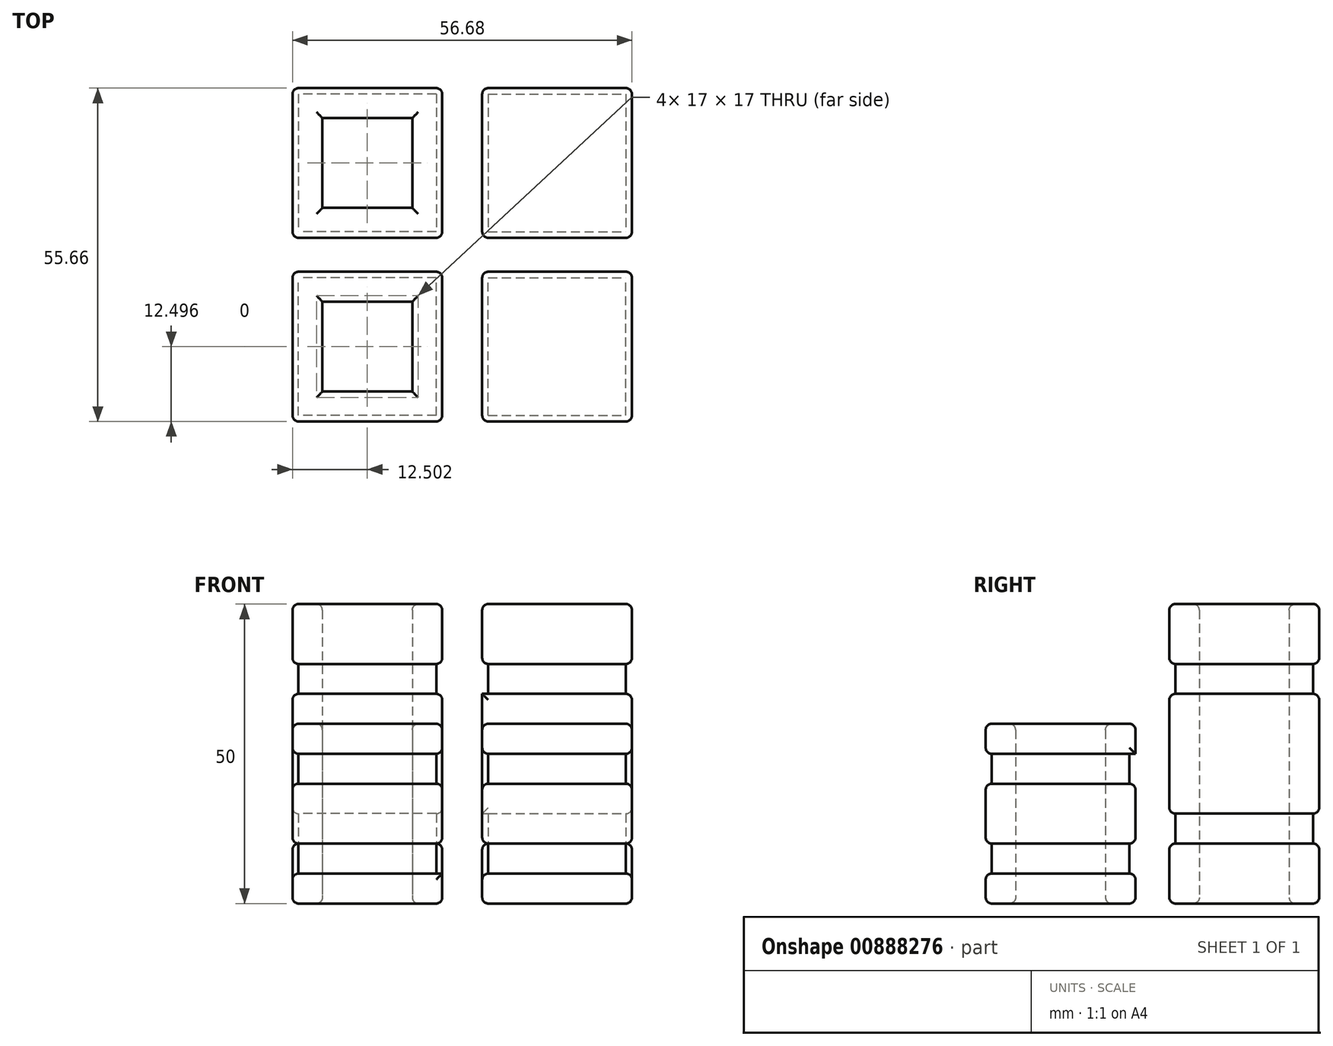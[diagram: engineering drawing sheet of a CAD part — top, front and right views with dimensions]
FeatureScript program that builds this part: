
annotation { "Feature Type Name" : "Feature", "Feature Type Description" : "" }
export const myFeature = defineFeature(function(context is Context, id is Id, definition is map)
    precondition{}
    {
        {
            var Q0;
            Q0=qCreatedBy(makeId("Top.planeOp"),FACE);
            var sketch = newSketch(context, id + "F0", { "sketchPlane" : qUnion([Q0])});
            skLineSegment(sketch, "E0.bottom", {"start": v(3.34, 2.83) * mm, "end": v(28.34, 2.83) * mm});
            skLineSegment(sketch, "E0.top", {"start": v(3.34, 27.83) * mm, "end": v(28.34, 27.83) * mm});
            skLineSegment(sketch, "E0.left", {"start": v(3.34, 2.83) * mm, "end": v(3.34, 27.83) * mm});
            skLineSegment(sketch, "E0.right", {"start": v(28.34, 2.83) * mm, "end": v(28.34, 27.83) * mm});
            skLineSegment(sketch, "E1.bottom", {"start": v(4.34, 26.83) * mm, "end": v(27.34, 26.83) * mm});
            skLineSegment(sketch, "E1.top", {"start": v(4.34, 3.83) * mm, "end": v(27.34, 3.83) * mm});
            skLineSegment(sketch, "E1.left", {"start": v(4.34, 26.83) * mm, "end": v(4.34, 3.83) * mm});
            skLineSegment(sketch, "E1.right", {"start": v(27.34, 26.83) * mm, "end": v(27.34, 3.83) * mm});
            skLineSegment(sketch, "E2.bottom", {"start": v(8.34, 22.83) * mm, "end": v(23.34, 22.83) * mm});
            skLineSegment(sketch, "E2.top", {"start": v(8.34, 7.83) * mm, "end": v(23.34, 7.83) * mm});
            skLineSegment(sketch, "E2.left", {"start": v(8.34, 22.83) * mm, "end": v(8.34, 7.83) * mm});
            skLineSegment(sketch, "E2.right", {"start": v(23.34, 22.83) * mm, "end": v(23.34, 7.83) * mm});
            skLineSegment(sketch, "E3.MirrorCS", {"start": v(-4.34, 3.83) * mm, "end": v(-27.34, 3.83) * mm});
            skLineSegment(sketch, "E4.MirrorCS", {"start": v(-3.34, 27.83) * mm, "end": v(-28.34, 27.83) * mm});
            skLineSegment(sketch, "E5.MirrorCS", {"start": v(-3.34, 2.83) * mm, "end": v(-3.34, 27.83) * mm});
            skLineSegment(sketch, "E6.MirrorCS", {"start": v(-23.34, 22.83) * mm, "end": v(-23.34, 7.83) * mm});
            skLineSegment(sketch, "E7.MirrorCS", {"start": v(-4.34, 26.83) * mm, "end": v(-27.34, 26.83) * mm});
            skLineSegment(sketch, "E8.MirrorCS", {"start": v(-27.34, 26.83) * mm, "end": v(-27.34, 3.83) * mm});
            skLineSegment(sketch, "E9.MirrorCS", {"start": v(-28.34, 2.83) * mm, "end": v(-28.34, 27.83) * mm});
            skLineSegment(sketch, "E10.MirrorCS", {"start": v(-8.34, 22.83) * mm, "end": v(-23.34, 22.83) * mm});
            skLineSegment(sketch, "E11.MirrorCS", {"start": v(-4.34, 26.83) * mm, "end": v(-4.34, 3.83) * mm});
            skLineSegment(sketch, "E12.MirrorCS", {"start": v(-8.34, 22.83) * mm, "end": v(-8.34, 7.83) * mm});
            skLineSegment(sketch, "E13.MirrorCS", {"start": v(-3.34, 2.83) * mm, "end": v(-28.34, 2.83) * mm});
            skLineSegment(sketch, "E14.MirrorCS", {"start": v(-8.34, 7.83) * mm, "end": v(-23.34, 7.83) * mm});
            skLineSegment(sketch, "E15.MirrorCS", {"start": v(-3.34, -27.83) * mm, "end": v(-28.34, -27.83) * mm});
            skLineSegment(sketch, "E16.MirrorCS", {"start": v(3.34, -2.83) * mm, "end": v(28.34, -2.83) * mm});
            skLineSegment(sketch, "E17.MirrorCS", {"start": v(3.34, -27.83) * mm, "end": v(28.34, -27.83) * mm});
            skLineSegment(sketch, "E18.MirrorCS", {"start": v(3.34, -2.83) * mm, "end": v(3.34, -27.83) * mm});
            skLineSegment(sketch, "E19.MirrorCS", {"start": v(-8.34, -7.83) * mm, "end": v(-23.34, -7.83) * mm});
            skLineSegment(sketch, "E20.MirrorCS", {"start": v(28.34, -2.83) * mm, "end": v(28.34, -27.83) * mm});
            skLineSegment(sketch, "E21.MirrorCS", {"start": v(-3.34, -2.83) * mm, "end": v(-28.34, -2.83) * mm});
            skLineSegment(sketch, "E22.MirrorCS", {"start": v(4.34, -26.83) * mm, "end": v(27.34, -26.83) * mm});
            skLineSegment(sketch, "E23.MirrorCS", {"start": v(4.34, -3.83) * mm, "end": v(27.34, -3.83) * mm});
            skLineSegment(sketch, "E24.MirrorCS", {"start": v(-8.34, -22.83) * mm, "end": v(-8.34, -7.83) * mm});
            skLineSegment(sketch, "E25.MirrorCS", {"start": v(-4.34, -26.83) * mm, "end": v(-4.34, -3.83) * mm});
            skLineSegment(sketch, "E26.MirrorCS", {"start": v(-4.34, -3.83) * mm, "end": v(-27.34, -3.83) * mm});
            skLineSegment(sketch, "E27.MirrorCS", {"start": v(-4.34, -26.83) * mm, "end": v(-27.34, -26.83) * mm});
            skLineSegment(sketch, "E28.MirrorCS", {"start": v(8.34, -7.83) * mm, "end": v(23.34, -7.83) * mm});
            skLineSegment(sketch, "E29.MirrorCS", {"start": v(23.34, -22.83) * mm, "end": v(23.34, -7.83) * mm});
            skLineSegment(sketch, "E30.MirrorCS", {"start": v(-27.34, -26.83) * mm, "end": v(-27.34, -3.83) * mm});
            skLineSegment(sketch, "E31.MirrorCS", {"start": v(-23.34, -22.83) * mm, "end": v(-23.34, -7.83) * mm});
            skLineSegment(sketch, "E32.MirrorCS", {"start": v(-3.34, -2.83) * mm, "end": v(-3.34, -27.83) * mm});
            skLineSegment(sketch, "E33.MirrorCS", {"start": v(8.34, -22.83) * mm, "end": v(8.34, -7.83) * mm});
            skLineSegment(sketch, "E34.MirrorCS", {"start": v(-8.34, -22.83) * mm, "end": v(-23.34, -22.83) * mm});
            skLineSegment(sketch, "E35.MirrorCS", {"start": v(4.34, -26.83) * mm, "end": v(4.34, -3.83) * mm});
            skLineSegment(sketch, "E36.MirrorCS", {"start": v(-28.34, -2.83) * mm, "end": v(-28.34, -27.83) * mm});
            skLineSegment(sketch, "E37.MirrorCS", {"start": v(27.34, -26.83) * mm, "end": v(27.34, -3.83) * mm});
            skLineSegment(sketch, "E38.MirrorCS", {"start": v(8.34, -22.83) * mm, "end": v(23.34, -22.83) * mm});
            skSolve(sketch);
        }
        {
            var Q0;
            Q0=makeQuery(id+"F0.imprint","IMPRINT",FACE,{"disambiguationData":[TD([[makeQuery(id+"F0.imprint","IMPRINT",EDGE,{"derivedFrom":sQuery(id+"F0.wireOp",EDGE,"E0.bottom")}),1.0]])]});
            var Q1;
            Q1=makeQuery(id+"F0.imprint","IMPRINT",FACE,{"disambiguationData":[TD([[makeQuery(id+"F0.imprint","IMPRINT",EDGE,{"derivedFrom":sQuery(id+"F0.wireOp",EDGE,"E3.MirrorCS")}),1.0]])]});
            var Q2;
            Q2=makeQuery(id+"F0.imprint","IMPRINT",FACE,{"disambiguationData":[TD([[makeQuery(id+"F0.imprint","IMPRINT",EDGE,{"derivedFrom":sQuery(id+"F0.wireOp",EDGE,"E3.MirrorCS")}),-1.0]])]});
            var Q3;
            Q3=makeQuery(id+"F0.imprint","IMPRINT",FACE,{"disambiguationData":[TD([[makeQuery(id+"F0.imprint","IMPRINT",EDGE,{"derivedFrom":sQuery(id+"F0.wireOp",EDGE,"E1.bottom")}),-1.0]])]});
            var Q4;
            Q4=makeQuery(id+"F0.imprint","IMPRINT",FACE,{"disambiguationData":[TD([[makeQuery(id+"F0.imprint","IMPRINT",EDGE,{"derivedFrom":sQuery(id+"F0.wireOp",EDGE,"E2.bottom")}),-1.0]])]});
            extrude(context, id + "F1", {"entities" : qUnion([Q0, Q1, Q2, Q3, Q4]), "depth" : 50 * mm, "offsetDistance" : 25 * mm});
        }
        {
            var Q0;
            Q0=makeQuery(id+"F0.imprint","IMPRINT",FACE,{"disambiguationData":[TD([[makeQuery(id+"F0.imprint","IMPRINT",EDGE,{"derivedFrom":sQuery(id+"F0.wireOp",EDGE,"E15.MirrorCS")}),-1.0]])]});
            var Q1;
            Q1=makeQuery(id+"F0.imprint","IMPRINT",FACE,{"disambiguationData":[TD([[makeQuery(id+"F0.imprint","IMPRINT",EDGE,{"derivedFrom":sQuery(id+"F0.wireOp",EDGE,"E19.MirrorCS")}),-1.0]])]});
            var Q2;
            Q2=makeQuery(id+"F0.imprint","IMPRINT",FACE,{"disambiguationData":[TD([[makeQuery(id+"F0.imprint","IMPRINT",EDGE,{"derivedFrom":sQuery(id+"F0.wireOp",EDGE,"E16.MirrorCS")}),-1.0]])]});
            var Q3;
            Q3=makeQuery(id+"F0.imprint","IMPRINT",FACE,{"disambiguationData":[TD([[makeQuery(id+"F0.imprint","IMPRINT",EDGE,{"derivedFrom":sQuery(id+"F0.wireOp",EDGE,"E22.MirrorCS")}),1.0]])]});
            var Q4;
            Q4=makeQuery(id+"F0.imprint","IMPRINT",FACE,{"disambiguationData":[TD([[makeQuery(id+"F0.imprint","IMPRINT",EDGE,{"derivedFrom":sQuery(id+"F0.wireOp",EDGE,"E28.MirrorCS")}),-1.0]])]});
            extrude(context, id + "F2", {"entities" : qUnion([Q0, Q1, Q2, Q3, Q4]), "depth" : 30 * mm, "offsetDistance" : 25 * mm});
        }
        {
            var Q0;
            Q0=makeQuery(id+"F0.imprint","IMPRINT",FACE,{"disambiguationData":[TD([[makeQuery(id+"F0.imprint","IMPRINT",EDGE,{"derivedFrom":sQuery(id+"F0.wireOp",EDGE,"E15.MirrorCS")}),-1.0]])]});
            var Q1;
            Q1=makeQuery(id+"F0.imprint","IMPRINT",FACE,{"disambiguationData":[TD([[makeQuery(id+"F0.imprint","IMPRINT",EDGE,{"derivedFrom":sQuery(id+"F0.wireOp",EDGE,"E16.MirrorCS")}),-1.0]])]});
            extrude(context, id + "F3", {"entities" : qUnion([Q0, Q1]), "operationType" : NewBodyOperationType.REMOVE, "depth" : 25 * mm, "offsetDistance" : 25 * mm, "hasSecondDirection" : true, "secondDirectionOppositeDirection" : false, "secondDirectionDepth" : 20 * mm});
        }
        {
            var Q0;
            Q0=makeQuery(id+"F0.imprint","IMPRINT",FACE,{"disambiguationData":[TD([[makeQuery(id+"F0.imprint","IMPRINT",EDGE,{"derivedFrom":sQuery(id+"F0.wireOp",EDGE,"E15.MirrorCS")}),-1.0]])]});
            var Q1;
            Q1=makeQuery(id+"F0.imprint","IMPRINT",FACE,{"disambiguationData":[TD([[makeQuery(id+"F0.imprint","IMPRINT",EDGE,{"derivedFrom":sQuery(id+"F0.wireOp",EDGE,"E16.MirrorCS")}),-1.0]])]});
            extrude(context, id + "F4", {"entities" : qUnion([Q0, Q1]), "operationType" : NewBodyOperationType.REMOVE, "depth" : 10 * mm, "offsetDistance" : 25 * mm, "hasSecondDirection" : true, "secondDirectionOppositeDirection" : false, "secondDirectionDepth" : 5 * mm});
        }
        {
            var Q0;
            Q0=makeQuery(id+"F0.imprint","IMPRINT",FACE,{"disambiguationData":[TD([[makeQuery(id+"F0.imprint","IMPRINT",EDGE,{"derivedFrom":sQuery(id+"F0.wireOp",EDGE,"E0.bottom")}),1.0]])]});
            var Q1;
            Q1=makeQuery(id+"F0.imprint","IMPRINT",FACE,{"disambiguationData":[TD([[makeQuery(id+"F0.imprint","IMPRINT",EDGE,{"derivedFrom":sQuery(id+"F0.wireOp",EDGE,"E3.MirrorCS")}),1.0]])]});
            extrude(context, id + "F5", {"entities" : qUnion([Q0, Q1]), "operationType" : NewBodyOperationType.REMOVE, "depth" : 40 * mm, "offsetDistance" : 25 * mm, "hasSecondDirection" : true, "secondDirectionOppositeDirection" : false, "secondDirectionDepth" : 35 * mm});
        }
        {
            var Q0;
            Q0=makeQuery(id+"F0.imprint","IMPRINT",FACE,{"disambiguationData":[TD([[makeQuery(id+"F0.imprint","IMPRINT",EDGE,{"derivedFrom":sQuery(id+"F0.wireOp",EDGE,"E0.bottom")}),1.0]])]});
            var Q1;
            Q1=makeQuery(id+"F0.imprint","IMPRINT",FACE,{"disambiguationData":[TD([[makeQuery(id+"F0.imprint","IMPRINT",EDGE,{"derivedFrom":sQuery(id+"F0.wireOp",EDGE,"E3.MirrorCS")}),1.0]])]});
            extrude(context, id + "F6", {"entities" : qUnion([Q0, Q1]), "operationType" : NewBodyOperationType.REMOVE, "depth" : 15 * mm, "offsetDistance" : 25 * mm, "hasSecondDirection" : true, "secondDirectionOppositeDirection" : false, "secondDirectionDepth" : 10 * mm});
        }
        {
            var Q0;
            {var subQ0=sQuery(id+"F0.wireOp",EDGE,"E0.right");var subQ1=sQuery(id+"F0.wireOp",EDGE,"E0.left");var subQ2=sQuery(id+"F0.wireOp",EDGE,"E0.top");var subQ3=sQuery(id+"F0.wireOp",EDGE,"E0.bottom");Q0=makeQuery(id+"F5.boolean.opBoolean","SPLIT",FACE,{"disambiguationData":[TD([makeQuery(id+"F1.opExtrude","CAP_FACE",FACE,{"disambiguationData":[OSD([subQ3,subQ2,subQ1,subQ0])],"isStart":false})])],"derivedFrom":makeQuery(id+"F1.opExtrude","SWEPT_FACE",FACE,{"disambiguationData":[OSD([subQ2])]})});}
            var Q1;
            {var subQ0=sQuery(id+"F0.wireOp",EDGE,"E0.bottom");var subQ1=sQuery(id+"F0.wireOp",EDGE,"E0.right");var subQ2=sQuery(id+"F0.wireOp",EDGE,"E0.left");var subQ3=sQuery(id+"F0.wireOp",EDGE,"E0.top");Q1=makeQuery(id+"F5.boolean.opBoolean","SPLIT",FACE,{"disambiguationData":[TD([makeQuery(id+"F1.opExtrude","CAP_FACE",FACE,{"disambiguationData":[OSD([subQ0,subQ3,subQ2,subQ1])],"isStart":false})])],"derivedFrom":makeQuery(id+"F1.opExtrude","SWEPT_FACE",FACE,{"disambiguationData":[OSD([subQ1])]})});}
            var Q2;
            {var subQ0=sQuery(id+"F0.wireOp",EDGE,"E0.right");var subQ1=sQuery(id+"F0.wireOp",EDGE,"E0.left");var subQ2=sQuery(id+"F0.wireOp",EDGE,"E0.top");var subQ3=sQuery(id+"F0.wireOp",EDGE,"E0.bottom");Q2=makeQuery(id+"F5.boolean.opBoolean","SPLIT",FACE,{"disambiguationData":[TD([makeQuery(id+"F1.opExtrude","CAP_FACE",FACE,{"disambiguationData":[OSD([subQ3,subQ2,subQ1,subQ0])],"isStart":false})])],"derivedFrom":makeQuery(id+"F1.opExtrude","SWEPT_FACE",FACE,{"disambiguationData":[OSD([subQ3])]})});}
            var Q3;
            {var subQ0=sQuery(id+"F0.wireOp",EDGE,"E0.bottom");var subQ1=sQuery(id+"F0.wireOp",EDGE,"E0.right");var subQ2=sQuery(id+"F0.wireOp",EDGE,"E0.left");var subQ3=sQuery(id+"F0.wireOp",EDGE,"E0.top");Q3=makeQuery(id+"F5.boolean.opBoolean","SPLIT",FACE,{"disambiguationData":[TD([makeQuery(id+"F1.opExtrude","CAP_FACE",FACE,{"disambiguationData":[OSD([subQ0,subQ3,subQ2,subQ1])],"isStart":false})])],"derivedFrom":makeQuery(id+"F1.opExtrude","SWEPT_FACE",FACE,{"disambiguationData":[OSD([subQ2])]})});}
            var Q4;
            {var subQ0=sQuery(id+"F0.wireOp",EDGE,"E0.bottom");var subQ2=sQuery(id+"F0.wireOp",EDGE,"E1.right");var subQ3=sQuery(id+"F0.wireOp",EDGE,"E1.left");var subQ4=sQuery(id+"F0.wireOp",EDGE,"E1.top");var subQ5=sQuery(id+"F0.wireOp",EDGE,"E1.bottom");var subQ6=sQuery(id+"F0.wireOp",EDGE,"E0.right");var subQ7=sQuery(id+"F0.wireOp",EDGE,"E0.left");var subQ8=sQuery(id+"F0.wireOp",EDGE,"E0.top");var subQ10=makeQuery(id+"F5.opExtrude","CAP_FACE",FACE,{"disambiguationData":[OSD([subQ0,subQ8,subQ7,subQ6,subQ5,subQ4,subQ3,subQ2])],"isStart":true});Q4=makeQuery(id+"F6.boolean.opBoolean","SPLIT",EDGE,{"disambiguationData":[TD([makeQuery(id+"F5.boolean.opBoolean","COPY",FACE,{"derivedFrom":subQ10})])],"derivedFrom":makeQuery(id+"F5.boolean.opBoolean","SPLIT",EDGE,{"disambiguationData":[TD([makeQuery(id+"F1.opExtrude","CAP_FACE",FACE,{"disambiguationData":[OSD([subQ0,subQ8,subQ7,subQ6])],"isStart":true})])],"derivedFrom":makeQuery(id+"F1.opExtrude","SWEPT_EDGE",EDGE,{"disambiguationData":[OSD([subQ0,subQ7])]})})});}
            var Q5;
            {var subQ0=sQuery(id+"F0.wireOp",EDGE,"E0.left");var subQ2=sQuery(id+"F0.wireOp",EDGE,"E0.right");var subQ4=sQuery(id+"F0.wireOp",EDGE,"E1.right");var subQ5=sQuery(id+"F0.wireOp",EDGE,"E1.left");var subQ6=sQuery(id+"F0.wireOp",EDGE,"E1.top");var subQ7=sQuery(id+"F0.wireOp",EDGE,"E1.bottom");var subQ8=sQuery(id+"F0.wireOp",EDGE,"E0.top");var subQ9=sQuery(id+"F0.wireOp",EDGE,"E0.bottom");var subQ10=makeQuery(id+"F5.opExtrude","CAP_FACE",FACE,{"disambiguationData":[OSD([subQ9,subQ8,subQ0,subQ2,subQ7,subQ6,subQ5,subQ4])],"isStart":true});Q5=makeQuery(id+"F6.boolean.opBoolean","SPLIT",FACE,{"disambiguationData":[TD([makeQuery(id+"F5.boolean.opBoolean","COPY",FACE,{"derivedFrom":subQ10})])],"derivedFrom":makeQuery(id+"F5.boolean.opBoolean","SPLIT",FACE,{"disambiguationData":[TD([makeQuery(id+"F1.opExtrude","CAP_FACE",FACE,{"disambiguationData":[OSD([subQ9,subQ8,subQ0,subQ2])],"isStart":true})])],"derivedFrom":makeQuery(id+"F1.opExtrude","SWEPT_FACE",FACE,{"disambiguationData":[OSD([subQ9])]})})});}
            var Q6;
            {var subQ0=sQuery(id+"F0.wireOp",EDGE,"E0.bottom");var subQ2=sQuery(id+"F0.wireOp",EDGE,"E1.right");var subQ3=sQuery(id+"F0.wireOp",EDGE,"E1.left");var subQ4=sQuery(id+"F0.wireOp",EDGE,"E1.top");var subQ5=sQuery(id+"F0.wireOp",EDGE,"E1.bottom");var subQ6=sQuery(id+"F0.wireOp",EDGE,"E0.right");var subQ7=sQuery(id+"F0.wireOp",EDGE,"E0.left");var subQ8=sQuery(id+"F0.wireOp",EDGE,"E0.top");var subQ10=makeQuery(id+"F5.opExtrude","CAP_FACE",FACE,{"disambiguationData":[OSD([subQ0,subQ8,subQ7,subQ6,subQ5,subQ4,subQ3,subQ2])],"isStart":true});Q6=makeQuery(id+"F6.boolean.opBoolean","SPLIT",FACE,{"disambiguationData":[TD([makeQuery(id+"F5.boolean.opBoolean","COPY",FACE,{"derivedFrom":subQ10})])],"derivedFrom":makeQuery(id+"F5.boolean.opBoolean","SPLIT",FACE,{"disambiguationData":[TD([makeQuery(id+"F1.opExtrude","CAP_FACE",FACE,{"disambiguationData":[OSD([subQ0,subQ8,subQ7,subQ6])],"isStart":true})])],"derivedFrom":makeQuery(id+"F1.opExtrude","SWEPT_FACE",FACE,{"disambiguationData":[OSD([subQ6])]})})});}
            var Q7;
            {var subQ0=sQuery(id+"F0.wireOp",EDGE,"E0.left");var subQ2=sQuery(id+"F0.wireOp",EDGE,"E0.right");var subQ4=sQuery(id+"F0.wireOp",EDGE,"E1.right");var subQ5=sQuery(id+"F0.wireOp",EDGE,"E1.left");var subQ6=sQuery(id+"F0.wireOp",EDGE,"E1.top");var subQ7=sQuery(id+"F0.wireOp",EDGE,"E1.bottom");var subQ8=sQuery(id+"F0.wireOp",EDGE,"E0.top");var subQ9=sQuery(id+"F0.wireOp",EDGE,"E0.bottom");var subQ10=makeQuery(id+"F5.opExtrude","CAP_FACE",FACE,{"disambiguationData":[OSD([subQ9,subQ8,subQ0,subQ2,subQ7,subQ6,subQ5,subQ4])],"isStart":true});Q7=makeQuery(id+"F6.boolean.opBoolean","SPLIT",FACE,{"disambiguationData":[TD([makeQuery(id+"F5.boolean.opBoolean","COPY",FACE,{"derivedFrom":subQ10})])],"derivedFrom":makeQuery(id+"F5.boolean.opBoolean","SPLIT",FACE,{"disambiguationData":[TD([makeQuery(id+"F1.opExtrude","CAP_FACE",FACE,{"disambiguationData":[OSD([subQ9,subQ8,subQ0,subQ2])],"isStart":true})])],"derivedFrom":makeQuery(id+"F1.opExtrude","SWEPT_FACE",FACE,{"disambiguationData":[OSD([subQ8])]})})});}
            var Q8;
            {var subQ0=sQuery(id+"F0.wireOp",EDGE,"E0.bottom");var subQ2=sQuery(id+"F0.wireOp",EDGE,"E0.right");var subQ3=sQuery(id+"F0.wireOp",EDGE,"E0.left");var subQ4=sQuery(id+"F0.wireOp",EDGE,"E0.top");var subQ5=makeQuery(id+"F1.opExtrude","CAP_FACE",FACE,{"disambiguationData":[OSD([subQ0,subQ4,subQ3,subQ2])],"isStart":true});Q8=makeQuery(id+"F6.boolean.opBoolean","SPLIT",FACE,{"disambiguationData":[TD([subQ5])],"derivedFrom":makeQuery(id+"F5.boolean.opBoolean","SPLIT",FACE,{"disambiguationData":[TD([subQ5])],"derivedFrom":makeQuery(id+"F1.opExtrude","SWEPT_FACE",FACE,{"disambiguationData":[OSD([subQ2])]})})});}
            var Q9;
            {var subQ0=sQuery(id+"F0.wireOp",EDGE,"E0.right");var subQ1=sQuery(id+"F0.wireOp",EDGE,"E0.left");var subQ2=sQuery(id+"F0.wireOp",EDGE,"E0.top");var subQ3=sQuery(id+"F0.wireOp",EDGE,"E0.bottom");var subQ4=makeQuery(id+"F1.opExtrude","CAP_FACE",FACE,{"disambiguationData":[OSD([subQ3,subQ2,subQ1,subQ0])],"isStart":true});Q9=makeQuery(id+"F6.boolean.opBoolean","SPLIT",FACE,{"disambiguationData":[TD([subQ4])],"derivedFrom":makeQuery(id+"F5.boolean.opBoolean","SPLIT",FACE,{"disambiguationData":[TD([subQ4])],"derivedFrom":makeQuery(id+"F1.opExtrude","SWEPT_FACE",FACE,{"disambiguationData":[OSD([subQ2])]})})});}
            var Q10;
            {var subQ0=sQuery(id+"F0.wireOp",EDGE,"E0.right");var subQ1=sQuery(id+"F0.wireOp",EDGE,"E0.left");var subQ2=sQuery(id+"F0.wireOp",EDGE,"E0.top");var subQ3=sQuery(id+"F0.wireOp",EDGE,"E0.bottom");var subQ4=makeQuery(id+"F1.opExtrude","CAP_FACE",FACE,{"disambiguationData":[OSD([subQ3,subQ2,subQ1,subQ0])],"isStart":true});Q10=makeQuery(id+"F6.boolean.opBoolean","SPLIT",FACE,{"disambiguationData":[TD([subQ4])],"derivedFrom":makeQuery(id+"F5.boolean.opBoolean","SPLIT",FACE,{"disambiguationData":[TD([subQ4])],"derivedFrom":makeQuery(id+"F1.opExtrude","SWEPT_FACE",FACE,{"disambiguationData":[OSD([subQ3])]})})});}
            var Q11;
            {var subQ0=sQuery(id+"F0.wireOp",EDGE,"E0.bottom");var subQ2=sQuery(id+"F0.wireOp",EDGE,"E0.right");var subQ3=sQuery(id+"F0.wireOp",EDGE,"E0.left");var subQ4=sQuery(id+"F0.wireOp",EDGE,"E0.top");var subQ5=makeQuery(id+"F1.opExtrude","CAP_FACE",FACE,{"disambiguationData":[OSD([subQ0,subQ4,subQ3,subQ2])],"isStart":true});Q11=makeQuery(id+"F6.boolean.opBoolean","SPLIT",FACE,{"disambiguationData":[TD([subQ5])],"derivedFrom":makeQuery(id+"F5.boolean.opBoolean","SPLIT",FACE,{"disambiguationData":[TD([subQ5])],"derivedFrom":makeQuery(id+"F1.opExtrude","SWEPT_FACE",FACE,{"disambiguationData":[OSD([subQ3])]})})});}
            var Q12;
            Q12=makeQuery(id+"F1.opExtrude","CAP_FACE",FACE,{"disambiguationData":[OSD([sQuery(id+"F0.wireOp",EDGE,"E4.MirrorCS"),sQuery(id+"F0.wireOp",EDGE,"E5.MirrorCS"),sQuery(id+"F0.wireOp",EDGE,"E6.MirrorCS"),sQuery(id+"F0.wireOp",EDGE,"E9.MirrorCS"),sQuery(id+"F0.wireOp",EDGE,"E10.MirrorCS"),sQuery(id+"F0.wireOp",EDGE,"E12.MirrorCS"),sQuery(id+"F0.wireOp",EDGE,"E13.MirrorCS"),sQuery(id+"F0.wireOp",EDGE,"E14.MirrorCS")])],"isStart":true});
            var Q13;
            {var subQ0=sQuery(id+"F0.wireOp",EDGE,"E4.MirrorCS");var subQ2=sQuery(id+"F0.wireOp",EDGE,"E13.MirrorCS");var subQ3=sQuery(id+"F0.wireOp",EDGE,"E9.MirrorCS");var subQ4=sQuery(id+"F0.wireOp",EDGE,"E5.MirrorCS");var subQ5=makeQuery(id+"F1.opExtrude","CAP_FACE",FACE,{"disambiguationData":[OSD([subQ0,subQ4,sQuery(id+"F0.wireOp",EDGE,"E6.MirrorCS"),subQ3,sQuery(id+"F0.wireOp",EDGE,"E10.MirrorCS"),sQuery(id+"F0.wireOp",EDGE,"E12.MirrorCS"),subQ2,sQuery(id+"F0.wireOp",EDGE,"E14.MirrorCS")])],"isStart":true});Q13=makeQuery(id+"F6.boolean.opBoolean","SPLIT",FACE,{"disambiguationData":[TD([subQ5])],"derivedFrom":makeQuery(id+"F5.boolean.opBoolean","SPLIT",FACE,{"disambiguationData":[TD([subQ5])],"derivedFrom":makeQuery(id+"F1.opExtrude","SWEPT_FACE",FACE,{"disambiguationData":[OSD([subQ3])]})})});}
            var Q14;
            {var subQ0=sQuery(id+"F0.wireOp",EDGE,"E4.MirrorCS");var subQ2=sQuery(id+"F0.wireOp",EDGE,"E13.MirrorCS");var subQ3=sQuery(id+"F0.wireOp",EDGE,"E9.MirrorCS");var subQ4=sQuery(id+"F0.wireOp",EDGE,"E5.MirrorCS");var subQ5=makeQuery(id+"F1.opExtrude","CAP_FACE",FACE,{"disambiguationData":[OSD([subQ0,subQ4,sQuery(id+"F0.wireOp",EDGE,"E6.MirrorCS"),subQ3,sQuery(id+"F0.wireOp",EDGE,"E10.MirrorCS"),sQuery(id+"F0.wireOp",EDGE,"E12.MirrorCS"),subQ2,sQuery(id+"F0.wireOp",EDGE,"E14.MirrorCS")])],"isStart":true});Q14=makeQuery(id+"F6.boolean.opBoolean","SPLIT",FACE,{"disambiguationData":[TD([subQ5])],"derivedFrom":makeQuery(id+"F5.boolean.opBoolean","SPLIT",FACE,{"disambiguationData":[TD([subQ5])],"derivedFrom":makeQuery(id+"F1.opExtrude","SWEPT_FACE",FACE,{"disambiguationData":[OSD([subQ4])]})})});}
            var Q15;
            {var subQ0=sQuery(id+"F0.wireOp",EDGE,"E13.MirrorCS");var subQ1=sQuery(id+"F0.wireOp",EDGE,"E9.MirrorCS");var subQ2=sQuery(id+"F0.wireOp",EDGE,"E5.MirrorCS");var subQ3=sQuery(id+"F0.wireOp",EDGE,"E4.MirrorCS");var subQ4=makeQuery(id+"F1.opExtrude","CAP_FACE",FACE,{"disambiguationData":[OSD([subQ3,subQ2,sQuery(id+"F0.wireOp",EDGE,"E6.MirrorCS"),subQ1,sQuery(id+"F0.wireOp",EDGE,"E10.MirrorCS"),sQuery(id+"F0.wireOp",EDGE,"E12.MirrorCS"),subQ0,sQuery(id+"F0.wireOp",EDGE,"E14.MirrorCS")])],"isStart":true});Q15=makeQuery(id+"F6.boolean.opBoolean","SPLIT",FACE,{"disambiguationData":[TD([subQ4])],"derivedFrom":makeQuery(id+"F5.boolean.opBoolean","SPLIT",FACE,{"disambiguationData":[TD([subQ4])],"derivedFrom":makeQuery(id+"F1.opExtrude","SWEPT_FACE",FACE,{"disambiguationData":[OSD([subQ3])]})})});}
            var Q16;
            {var subQ0=sQuery(id+"F0.wireOp",EDGE,"E13.MirrorCS");var subQ1=sQuery(id+"F0.wireOp",EDGE,"E9.MirrorCS");var subQ2=sQuery(id+"F0.wireOp",EDGE,"E5.MirrorCS");var subQ3=sQuery(id+"F0.wireOp",EDGE,"E4.MirrorCS");var subQ4=makeQuery(id+"F1.opExtrude","CAP_FACE",FACE,{"disambiguationData":[OSD([subQ3,subQ2,sQuery(id+"F0.wireOp",EDGE,"E6.MirrorCS"),subQ1,sQuery(id+"F0.wireOp",EDGE,"E10.MirrorCS"),sQuery(id+"F0.wireOp",EDGE,"E12.MirrorCS"),subQ0,sQuery(id+"F0.wireOp",EDGE,"E14.MirrorCS")])],"isStart":true});Q16=makeQuery(id+"F6.boolean.opBoolean","SPLIT",FACE,{"disambiguationData":[TD([subQ4])],"derivedFrom":makeQuery(id+"F5.boolean.opBoolean","SPLIT",FACE,{"disambiguationData":[TD([subQ4])],"derivedFrom":makeQuery(id+"F1.opExtrude","SWEPT_FACE",FACE,{"disambiguationData":[OSD([subQ0])]})})});}
            var Q17;
            {var subQ0=sQuery(id+"F0.wireOp",EDGE,"E5.MirrorCS");var subQ2=sQuery(id+"F0.wireOp",EDGE,"E13.MirrorCS");var subQ3=sQuery(id+"F0.wireOp",EDGE,"E11.MirrorCS");var subQ4=sQuery(id+"F0.wireOp",EDGE,"E9.MirrorCS");var subQ5=sQuery(id+"F0.wireOp",EDGE,"E8.MirrorCS");var subQ6=sQuery(id+"F0.wireOp",EDGE,"E7.MirrorCS");var subQ7=sQuery(id+"F0.wireOp",EDGE,"E4.MirrorCS");var subQ8=sQuery(id+"F0.wireOp",EDGE,"E3.MirrorCS");var subQ9=makeQuery(id+"F5.opExtrude","CAP_FACE",FACE,{"disambiguationData":[OSD([subQ8,subQ7,subQ0,subQ6,subQ5,subQ4,subQ3,subQ2])],"isStart":true});Q17=makeQuery(id+"F6.boolean.opBoolean","SPLIT",FACE,{"disambiguationData":[TD([makeQuery(id+"F5.boolean.opBoolean","COPY",FACE,{"derivedFrom":subQ9})])],"derivedFrom":makeQuery(id+"F5.boolean.opBoolean","SPLIT",FACE,{"disambiguationData":[TD([makeQuery(id+"F1.opExtrude","CAP_FACE",FACE,{"disambiguationData":[OSD([subQ7,subQ0,sQuery(id+"F0.wireOp",EDGE,"E6.MirrorCS"),subQ4,sQuery(id+"F0.wireOp",EDGE,"E10.MirrorCS"),sQuery(id+"F0.wireOp",EDGE,"E12.MirrorCS"),subQ2,sQuery(id+"F0.wireOp",EDGE,"E14.MirrorCS")])],"isStart":true})])],"derivedFrom":makeQuery(id+"F1.opExtrude","SWEPT_FACE",FACE,{"disambiguationData":[OSD([subQ2])]})})});}
            var Q18;
            {var subQ0=sQuery(id+"F0.wireOp",EDGE,"E4.MirrorCS");var subQ2=sQuery(id+"F0.wireOp",EDGE,"E13.MirrorCS");var subQ4=sQuery(id+"F0.wireOp",EDGE,"E11.MirrorCS");var subQ5=sQuery(id+"F0.wireOp",EDGE,"E9.MirrorCS");var subQ6=sQuery(id+"F0.wireOp",EDGE,"E8.MirrorCS");var subQ7=sQuery(id+"F0.wireOp",EDGE,"E7.MirrorCS");var subQ8=sQuery(id+"F0.wireOp",EDGE,"E5.MirrorCS");var subQ9=sQuery(id+"F0.wireOp",EDGE,"E3.MirrorCS");var subQ10=makeQuery(id+"F5.opExtrude","CAP_FACE",FACE,{"disambiguationData":[OSD([subQ9,subQ0,subQ8,subQ7,subQ6,subQ5,subQ4,subQ2])],"isStart":true});Q18=makeQuery(id+"F6.boolean.opBoolean","SPLIT",FACE,{"disambiguationData":[TD([makeQuery(id+"F5.boolean.opBoolean","COPY",FACE,{"derivedFrom":subQ10})])],"derivedFrom":makeQuery(id+"F5.boolean.opBoolean","SPLIT",FACE,{"disambiguationData":[TD([makeQuery(id+"F1.opExtrude","CAP_FACE",FACE,{"disambiguationData":[OSD([subQ0,subQ8,sQuery(id+"F0.wireOp",EDGE,"E6.MirrorCS"),subQ5,sQuery(id+"F0.wireOp",EDGE,"E10.MirrorCS"),sQuery(id+"F0.wireOp",EDGE,"E12.MirrorCS"),subQ2,sQuery(id+"F0.wireOp",EDGE,"E14.MirrorCS")])],"isStart":true})])],"derivedFrom":makeQuery(id+"F1.opExtrude","SWEPT_FACE",FACE,{"disambiguationData":[OSD([subQ5])]})})});}
            var Q19;
            {var subQ0=sQuery(id+"F0.wireOp",EDGE,"E13.MirrorCS");var subQ1=sQuery(id+"F0.wireOp",EDGE,"E9.MirrorCS");var subQ2=sQuery(id+"F0.wireOp",EDGE,"E5.MirrorCS");var subQ3=sQuery(id+"F0.wireOp",EDGE,"E4.MirrorCS");Q19=makeQuery(id+"F5.boolean.opBoolean","SPLIT",FACE,{"disambiguationData":[TD([makeQuery(id+"F1.opExtrude","CAP_FACE",FACE,{"disambiguationData":[OSD([subQ3,subQ2,sQuery(id+"F0.wireOp",EDGE,"E6.MirrorCS"),subQ1,sQuery(id+"F0.wireOp",EDGE,"E10.MirrorCS"),sQuery(id+"F0.wireOp",EDGE,"E12.MirrorCS"),subQ0,sQuery(id+"F0.wireOp",EDGE,"E14.MirrorCS")])],"isStart":false})])],"derivedFrom":makeQuery(id+"F1.opExtrude","SWEPT_FACE",FACE,{"disambiguationData":[OSD([subQ0])]})});}
            var Q20;
            {var subQ0=sQuery(id+"F0.wireOp",EDGE,"E4.MirrorCS");var subQ1=sQuery(id+"F0.wireOp",EDGE,"E13.MirrorCS");var subQ2=sQuery(id+"F0.wireOp",EDGE,"E9.MirrorCS");var subQ3=sQuery(id+"F0.wireOp",EDGE,"E5.MirrorCS");Q20=makeQuery(id+"F5.boolean.opBoolean","SPLIT",FACE,{"disambiguationData":[TD([makeQuery(id+"F1.opExtrude","CAP_FACE",FACE,{"disambiguationData":[OSD([subQ0,subQ3,sQuery(id+"F0.wireOp",EDGE,"E6.MirrorCS"),subQ2,sQuery(id+"F0.wireOp",EDGE,"E10.MirrorCS"),sQuery(id+"F0.wireOp",EDGE,"E12.MirrorCS"),subQ1,sQuery(id+"F0.wireOp",EDGE,"E14.MirrorCS")])],"isStart":false})])],"derivedFrom":makeQuery(id+"F1.opExtrude","SWEPT_FACE",FACE,{"disambiguationData":[OSD([subQ2])]})});}
            var Q21;
            Q21=makeQuery(id+"F1.opExtrude","CAP_FACE",FACE,{"disambiguationData":[OSD([sQuery(id+"F0.wireOp",EDGE,"E4.MirrorCS"),sQuery(id+"F0.wireOp",EDGE,"E5.MirrorCS"),sQuery(id+"F0.wireOp",EDGE,"E6.MirrorCS"),sQuery(id+"F0.wireOp",EDGE,"E9.MirrorCS"),sQuery(id+"F0.wireOp",EDGE,"E10.MirrorCS"),sQuery(id+"F0.wireOp",EDGE,"E12.MirrorCS"),sQuery(id+"F0.wireOp",EDGE,"E13.MirrorCS"),sQuery(id+"F0.wireOp",EDGE,"E14.MirrorCS")])],"isStart":false});
            var Q22;
            {var subQ0=sQuery(id+"F0.wireOp",EDGE,"E5.MirrorCS");var subQ2=sQuery(id+"F0.wireOp",EDGE,"E13.MirrorCS");var subQ3=sQuery(id+"F0.wireOp",EDGE,"E11.MirrorCS");var subQ4=sQuery(id+"F0.wireOp",EDGE,"E9.MirrorCS");var subQ5=sQuery(id+"F0.wireOp",EDGE,"E8.MirrorCS");var subQ6=sQuery(id+"F0.wireOp",EDGE,"E7.MirrorCS");var subQ7=sQuery(id+"F0.wireOp",EDGE,"E4.MirrorCS");var subQ8=sQuery(id+"F0.wireOp",EDGE,"E3.MirrorCS");var subQ9=makeQuery(id+"F5.opExtrude","CAP_FACE",FACE,{"disambiguationData":[OSD([subQ8,subQ7,subQ0,subQ6,subQ5,subQ4,subQ3,subQ2])],"isStart":true});Q22=makeQuery(id+"F6.boolean.opBoolean","SPLIT",FACE,{"disambiguationData":[TD([makeQuery(id+"F5.boolean.opBoolean","COPY",FACE,{"derivedFrom":subQ9})])],"derivedFrom":makeQuery(id+"F5.boolean.opBoolean","SPLIT",FACE,{"disambiguationData":[TD([makeQuery(id+"F1.opExtrude","CAP_FACE",FACE,{"disambiguationData":[OSD([subQ7,subQ0,sQuery(id+"F0.wireOp",EDGE,"E6.MirrorCS"),subQ4,sQuery(id+"F0.wireOp",EDGE,"E10.MirrorCS"),sQuery(id+"F0.wireOp",EDGE,"E12.MirrorCS"),subQ2,sQuery(id+"F0.wireOp",EDGE,"E14.MirrorCS")])],"isStart":true})])],"derivedFrom":makeQuery(id+"F1.opExtrude","SWEPT_FACE",FACE,{"disambiguationData":[OSD([subQ7])]})})});}
            var Q23;
            {var subQ0=sQuery(id+"F0.wireOp",EDGE,"E4.MirrorCS");var subQ2=sQuery(id+"F0.wireOp",EDGE,"E13.MirrorCS");var subQ4=sQuery(id+"F0.wireOp",EDGE,"E11.MirrorCS");var subQ5=sQuery(id+"F0.wireOp",EDGE,"E9.MirrorCS");var subQ6=sQuery(id+"F0.wireOp",EDGE,"E8.MirrorCS");var subQ7=sQuery(id+"F0.wireOp",EDGE,"E7.MirrorCS");var subQ8=sQuery(id+"F0.wireOp",EDGE,"E5.MirrorCS");var subQ9=sQuery(id+"F0.wireOp",EDGE,"E3.MirrorCS");var subQ10=makeQuery(id+"F5.opExtrude","CAP_FACE",FACE,{"disambiguationData":[OSD([subQ9,subQ0,subQ8,subQ7,subQ6,subQ5,subQ4,subQ2])],"isStart":true});Q23=makeQuery(id+"F6.boolean.opBoolean","SPLIT",FACE,{"disambiguationData":[TD([makeQuery(id+"F5.boolean.opBoolean","COPY",FACE,{"derivedFrom":subQ10})])],"derivedFrom":makeQuery(id+"F5.boolean.opBoolean","SPLIT",FACE,{"disambiguationData":[TD([makeQuery(id+"F1.opExtrude","CAP_FACE",FACE,{"disambiguationData":[OSD([subQ0,subQ8,sQuery(id+"F0.wireOp",EDGE,"E6.MirrorCS"),subQ5,sQuery(id+"F0.wireOp",EDGE,"E10.MirrorCS"),sQuery(id+"F0.wireOp",EDGE,"E12.MirrorCS"),subQ2,sQuery(id+"F0.wireOp",EDGE,"E14.MirrorCS")])],"isStart":true})])],"derivedFrom":makeQuery(id+"F1.opExtrude","SWEPT_FACE",FACE,{"disambiguationData":[OSD([subQ8])]})})});}
            var Q24;
            {var subQ0=sQuery(id+"F0.wireOp",EDGE,"E13.MirrorCS");var subQ1=sQuery(id+"F0.wireOp",EDGE,"E9.MirrorCS");var subQ2=sQuery(id+"F0.wireOp",EDGE,"E5.MirrorCS");var subQ3=sQuery(id+"F0.wireOp",EDGE,"E4.MirrorCS");Q24=makeQuery(id+"F5.boolean.opBoolean","SPLIT",FACE,{"disambiguationData":[TD([makeQuery(id+"F1.opExtrude","CAP_FACE",FACE,{"disambiguationData":[OSD([subQ3,subQ2,sQuery(id+"F0.wireOp",EDGE,"E6.MirrorCS"),subQ1,sQuery(id+"F0.wireOp",EDGE,"E10.MirrorCS"),sQuery(id+"F0.wireOp",EDGE,"E12.MirrorCS"),subQ0,sQuery(id+"F0.wireOp",EDGE,"E14.MirrorCS")])],"isStart":false})])],"derivedFrom":makeQuery(id+"F1.opExtrude","SWEPT_FACE",FACE,{"disambiguationData":[OSD([subQ3])]})});}
            var Q25;
            {var subQ0=sQuery(id+"F0.wireOp",EDGE,"E4.MirrorCS");var subQ1=sQuery(id+"F0.wireOp",EDGE,"E13.MirrorCS");var subQ2=sQuery(id+"F0.wireOp",EDGE,"E9.MirrorCS");var subQ3=sQuery(id+"F0.wireOp",EDGE,"E5.MirrorCS");Q25=makeQuery(id+"F5.boolean.opBoolean","SPLIT",FACE,{"disambiguationData":[TD([makeQuery(id+"F1.opExtrude","CAP_FACE",FACE,{"disambiguationData":[OSD([subQ0,subQ3,sQuery(id+"F0.wireOp",EDGE,"E6.MirrorCS"),subQ2,sQuery(id+"F0.wireOp",EDGE,"E10.MirrorCS"),sQuery(id+"F0.wireOp",EDGE,"E12.MirrorCS"),subQ1,sQuery(id+"F0.wireOp",EDGE,"E14.MirrorCS")])],"isStart":false})])],"derivedFrom":makeQuery(id+"F1.opExtrude","SWEPT_FACE",FACE,{"disambiguationData":[OSD([subQ3])]})});}
            fillet(context, id + "F7", {"entities" : qUnion([Q0, Q1, Q2, Q3, Q4, Q5, Q6, Q7, Q8, Q9, Q10, Q11, Q12, Q13, Q14, Q15, Q16, Q17, Q18, Q19, Q20, Q21, Q22, Q23, Q24, Q25]), "radius" : 1 * mm, "tangentPropagation" : true, "allowEdgeOverflow" : false});
        }
        {
            var Q0;
            {var subQ0=sQuery(id+"F0.wireOp",EDGE,"E32.MirrorCS");var subQ2=sQuery(id+"F0.wireOp",EDGE,"E36.MirrorCS");var subQ4=sQuery(id+"F0.wireOp",EDGE,"E30.MirrorCS");var subQ5=sQuery(id+"F0.wireOp",EDGE,"E27.MirrorCS");var subQ6=sQuery(id+"F0.wireOp",EDGE,"E26.MirrorCS");var subQ7=sQuery(id+"F0.wireOp",EDGE,"E25.MirrorCS");var subQ8=sQuery(id+"F0.wireOp",EDGE,"E21.MirrorCS");var subQ9=sQuery(id+"F0.wireOp",EDGE,"E15.MirrorCS");var subQ10=makeQuery(id+"F3.opExtrude","CAP_FACE",FACE,{"disambiguationData":[OSD([subQ9,subQ8,subQ7,subQ6,subQ5,subQ4,subQ0,subQ2])],"isStart":true});Q0=makeQuery(id+"F4.boolean.opBoolean","SPLIT",FACE,{"disambiguationData":[TD([makeQuery(id+"F3.boolean.opBoolean","COPY",FACE,{"derivedFrom":subQ10})])],"derivedFrom":makeQuery(id+"F3.boolean.opBoolean","SPLIT",FACE,{"disambiguationData":[TD([makeQuery(id+"F2.opExtrude","CAP_FACE",FACE,{"disambiguationData":[OSD([subQ9,sQuery(id+"F0.wireOp",EDGE,"E19.MirrorCS"),subQ8,sQuery(id+"F0.wireOp",EDGE,"E24.MirrorCS"),sQuery(id+"F0.wireOp",EDGE,"E31.MirrorCS"),subQ0,sQuery(id+"F0.wireOp",EDGE,"E34.MirrorCS"),subQ2])],"isStart":true})])],"derivedFrom":makeQuery(id+"F2.opExtrude","SWEPT_FACE",FACE,{"disambiguationData":[OSD([subQ8])]})})});}
            var Q1;
            {var subQ0=sQuery(id+"F0.wireOp",EDGE,"E15.MirrorCS");var subQ2=sQuery(id+"F0.wireOp",EDGE,"E21.MirrorCS");var subQ4=sQuery(id+"F0.wireOp",EDGE,"E36.MirrorCS");var subQ5=sQuery(id+"F0.wireOp",EDGE,"E32.MirrorCS");var subQ6=sQuery(id+"F0.wireOp",EDGE,"E30.MirrorCS");var subQ7=sQuery(id+"F0.wireOp",EDGE,"E27.MirrorCS");var subQ8=sQuery(id+"F0.wireOp",EDGE,"E26.MirrorCS");var subQ9=sQuery(id+"F0.wireOp",EDGE,"E25.MirrorCS");var subQ10=makeQuery(id+"F3.opExtrude","CAP_FACE",FACE,{"disambiguationData":[OSD([subQ0,subQ2,subQ9,subQ8,subQ7,subQ6,subQ5,subQ4])],"isStart":true});Q1=makeQuery(id+"F4.boolean.opBoolean","SPLIT",FACE,{"disambiguationData":[TD([makeQuery(id+"F3.boolean.opBoolean","COPY",FACE,{"derivedFrom":subQ10})])],"derivedFrom":makeQuery(id+"F3.boolean.opBoolean","SPLIT",FACE,{"disambiguationData":[TD([makeQuery(id+"F2.opExtrude","CAP_FACE",FACE,{"disambiguationData":[OSD([subQ0,sQuery(id+"F0.wireOp",EDGE,"E19.MirrorCS"),subQ2,sQuery(id+"F0.wireOp",EDGE,"E24.MirrorCS"),sQuery(id+"F0.wireOp",EDGE,"E31.MirrorCS"),subQ5,sQuery(id+"F0.wireOp",EDGE,"E34.MirrorCS"),subQ4])],"isStart":true})])],"derivedFrom":makeQuery(id+"F2.opExtrude","SWEPT_FACE",FACE,{"disambiguationData":[OSD([subQ5])]})})});}
            var Q2;
            {var subQ0=sQuery(id+"F0.wireOp",EDGE,"E36.MirrorCS");var subQ1=sQuery(id+"F0.wireOp",EDGE,"E32.MirrorCS");var subQ2=sQuery(id+"F0.wireOp",EDGE,"E21.MirrorCS");var subQ3=sQuery(id+"F0.wireOp",EDGE,"E15.MirrorCS");Q2=makeQuery(id+"F3.boolean.opBoolean","SPLIT",FACE,{"disambiguationData":[TD([makeQuery(id+"F2.opExtrude","CAP_FACE",FACE,{"disambiguationData":[OSD([subQ3,sQuery(id+"F0.wireOp",EDGE,"E19.MirrorCS"),subQ2,sQuery(id+"F0.wireOp",EDGE,"E24.MirrorCS"),sQuery(id+"F0.wireOp",EDGE,"E31.MirrorCS"),subQ1,sQuery(id+"F0.wireOp",EDGE,"E34.MirrorCS"),subQ0])],"isStart":false})])],"derivedFrom":makeQuery(id+"F2.opExtrude","SWEPT_FACE",FACE,{"disambiguationData":[OSD([subQ2])]})});}
            var Q3;
            {var subQ0=sQuery(id+"F0.wireOp",EDGE,"E15.MirrorCS");var subQ1=sQuery(id+"F0.wireOp",EDGE,"E21.MirrorCS");var subQ2=sQuery(id+"F0.wireOp",EDGE,"E36.MirrorCS");var subQ3=sQuery(id+"F0.wireOp",EDGE,"E32.MirrorCS");Q3=makeQuery(id+"F3.boolean.opBoolean","SPLIT",FACE,{"disambiguationData":[TD([makeQuery(id+"F2.opExtrude","CAP_FACE",FACE,{"disambiguationData":[OSD([subQ0,sQuery(id+"F0.wireOp",EDGE,"E19.MirrorCS"),subQ1,sQuery(id+"F0.wireOp",EDGE,"E24.MirrorCS"),sQuery(id+"F0.wireOp",EDGE,"E31.MirrorCS"),subQ3,sQuery(id+"F0.wireOp",EDGE,"E34.MirrorCS"),subQ2])],"isStart":false})])],"derivedFrom":makeQuery(id+"F2.opExtrude","SWEPT_FACE",FACE,{"disambiguationData":[OSD([subQ3])]})});}
            var Q4;
            Q4=makeQuery(id+"F2.opExtrude","CAP_FACE",FACE,{"disambiguationData":[OSD([sQuery(id+"F0.wireOp",EDGE,"E15.MirrorCS"),sQuery(id+"F0.wireOp",EDGE,"E19.MirrorCS"),sQuery(id+"F0.wireOp",EDGE,"E21.MirrorCS"),sQuery(id+"F0.wireOp",EDGE,"E24.MirrorCS"),sQuery(id+"F0.wireOp",EDGE,"E31.MirrorCS"),sQuery(id+"F0.wireOp",EDGE,"E32.MirrorCS"),sQuery(id+"F0.wireOp",EDGE,"E34.MirrorCS"),sQuery(id+"F0.wireOp",EDGE,"E36.MirrorCS")])],"isStart":false});
            var Q5;
            {var subQ0=sQuery(id+"F0.wireOp",EDGE,"E36.MirrorCS");var subQ1=sQuery(id+"F0.wireOp",EDGE,"E32.MirrorCS");var subQ2=sQuery(id+"F0.wireOp",EDGE,"E21.MirrorCS");var subQ3=sQuery(id+"F0.wireOp",EDGE,"E15.MirrorCS");var subQ4=makeQuery(id+"F2.opExtrude","CAP_FACE",FACE,{"disambiguationData":[OSD([subQ3,sQuery(id+"F0.wireOp",EDGE,"E19.MirrorCS"),subQ2,sQuery(id+"F0.wireOp",EDGE,"E24.MirrorCS"),sQuery(id+"F0.wireOp",EDGE,"E31.MirrorCS"),subQ1,sQuery(id+"F0.wireOp",EDGE,"E34.MirrorCS"),subQ0])],"isStart":true});Q5=makeQuery(id+"F4.boolean.opBoolean","SPLIT",FACE,{"disambiguationData":[TD([subQ4])],"derivedFrom":makeQuery(id+"F3.boolean.opBoolean","SPLIT",FACE,{"disambiguationData":[TD([subQ4])],"derivedFrom":makeQuery(id+"F2.opExtrude","SWEPT_FACE",FACE,{"disambiguationData":[OSD([subQ2])]})})});}
            var Q6;
            {var subQ0=sQuery(id+"F0.wireOp",EDGE,"E15.MirrorCS");var subQ2=sQuery(id+"F0.wireOp",EDGE,"E21.MirrorCS");var subQ4=sQuery(id+"F0.wireOp",EDGE,"E36.MirrorCS");var subQ5=sQuery(id+"F0.wireOp",EDGE,"E32.MirrorCS");var subQ6=makeQuery(id+"F2.opExtrude","CAP_FACE",FACE,{"disambiguationData":[OSD([subQ0,sQuery(id+"F0.wireOp",EDGE,"E19.MirrorCS"),subQ2,sQuery(id+"F0.wireOp",EDGE,"E24.MirrorCS"),sQuery(id+"F0.wireOp",EDGE,"E31.MirrorCS"),subQ5,sQuery(id+"F0.wireOp",EDGE,"E34.MirrorCS"),subQ4])],"isStart":true});Q6=makeQuery(id+"F4.boolean.opBoolean","SPLIT",FACE,{"disambiguationData":[TD([subQ6])],"derivedFrom":makeQuery(id+"F3.boolean.opBoolean","SPLIT",FACE,{"disambiguationData":[TD([subQ6])],"derivedFrom":makeQuery(id+"F2.opExtrude","SWEPT_FACE",FACE,{"disambiguationData":[OSD([subQ4])]})})});}
            var Q7;
            {var subQ0=sQuery(id+"F0.wireOp",EDGE,"E15.MirrorCS");var subQ2=sQuery(id+"F0.wireOp",EDGE,"E21.MirrorCS");var subQ4=sQuery(id+"F0.wireOp",EDGE,"E36.MirrorCS");var subQ5=sQuery(id+"F0.wireOp",EDGE,"E32.MirrorCS");var subQ6=sQuery(id+"F0.wireOp",EDGE,"E30.MirrorCS");var subQ7=sQuery(id+"F0.wireOp",EDGE,"E27.MirrorCS");var subQ8=sQuery(id+"F0.wireOp",EDGE,"E26.MirrorCS");var subQ9=sQuery(id+"F0.wireOp",EDGE,"E25.MirrorCS");var subQ10=makeQuery(id+"F3.opExtrude","CAP_FACE",FACE,{"disambiguationData":[OSD([subQ0,subQ2,subQ9,subQ8,subQ7,subQ6,subQ5,subQ4])],"isStart":true});Q7=makeQuery(id+"F4.boolean.opBoolean","SPLIT",FACE,{"disambiguationData":[TD([makeQuery(id+"F3.boolean.opBoolean","COPY",FACE,{"derivedFrom":subQ10})])],"derivedFrom":makeQuery(id+"F3.boolean.opBoolean","SPLIT",FACE,{"disambiguationData":[TD([makeQuery(id+"F2.opExtrude","CAP_FACE",FACE,{"disambiguationData":[OSD([subQ0,sQuery(id+"F0.wireOp",EDGE,"E19.MirrorCS"),subQ2,sQuery(id+"F0.wireOp",EDGE,"E24.MirrorCS"),sQuery(id+"F0.wireOp",EDGE,"E31.MirrorCS"),subQ5,sQuery(id+"F0.wireOp",EDGE,"E34.MirrorCS"),subQ4])],"isStart":true})])],"derivedFrom":makeQuery(id+"F2.opExtrude","SWEPT_FACE",FACE,{"disambiguationData":[OSD([subQ4])]})})});}
            var Q8;
            {var subQ0=sQuery(id+"F0.wireOp",EDGE,"E32.MirrorCS");var subQ2=sQuery(id+"F0.wireOp",EDGE,"E36.MirrorCS");var subQ4=sQuery(id+"F0.wireOp",EDGE,"E30.MirrorCS");var subQ5=sQuery(id+"F0.wireOp",EDGE,"E27.MirrorCS");var subQ6=sQuery(id+"F0.wireOp",EDGE,"E26.MirrorCS");var subQ7=sQuery(id+"F0.wireOp",EDGE,"E25.MirrorCS");var subQ8=sQuery(id+"F0.wireOp",EDGE,"E21.MirrorCS");var subQ9=sQuery(id+"F0.wireOp",EDGE,"E15.MirrorCS");var subQ10=makeQuery(id+"F3.opExtrude","CAP_FACE",FACE,{"disambiguationData":[OSD([subQ9,subQ8,subQ7,subQ6,subQ5,subQ4,subQ0,subQ2])],"isStart":true});Q8=makeQuery(id+"F4.boolean.opBoolean","SPLIT",FACE,{"disambiguationData":[TD([makeQuery(id+"F3.boolean.opBoolean","COPY",FACE,{"derivedFrom":subQ10})])],"derivedFrom":makeQuery(id+"F3.boolean.opBoolean","SPLIT",FACE,{"disambiguationData":[TD([makeQuery(id+"F2.opExtrude","CAP_FACE",FACE,{"disambiguationData":[OSD([subQ9,sQuery(id+"F0.wireOp",EDGE,"E19.MirrorCS"),subQ8,sQuery(id+"F0.wireOp",EDGE,"E24.MirrorCS"),sQuery(id+"F0.wireOp",EDGE,"E31.MirrorCS"),subQ0,sQuery(id+"F0.wireOp",EDGE,"E34.MirrorCS"),subQ2])],"isStart":true})])],"derivedFrom":makeQuery(id+"F2.opExtrude","SWEPT_FACE",FACE,{"disambiguationData":[OSD([subQ9])]})})});}
            var Q9;
            {var subQ0=sQuery(id+"F0.wireOp",EDGE,"E36.MirrorCS");var subQ1=sQuery(id+"F0.wireOp",EDGE,"E32.MirrorCS");var subQ2=sQuery(id+"F0.wireOp",EDGE,"E21.MirrorCS");var subQ3=sQuery(id+"F0.wireOp",EDGE,"E15.MirrorCS");var subQ4=makeQuery(id+"F2.opExtrude","CAP_FACE",FACE,{"disambiguationData":[OSD([subQ3,sQuery(id+"F0.wireOp",EDGE,"E19.MirrorCS"),subQ2,sQuery(id+"F0.wireOp",EDGE,"E24.MirrorCS"),sQuery(id+"F0.wireOp",EDGE,"E31.MirrorCS"),subQ1,sQuery(id+"F0.wireOp",EDGE,"E34.MirrorCS"),subQ0])],"isStart":true});Q9=makeQuery(id+"F4.boolean.opBoolean","SPLIT",FACE,{"disambiguationData":[TD([subQ4])],"derivedFrom":makeQuery(id+"F3.boolean.opBoolean","SPLIT",FACE,{"disambiguationData":[TD([subQ4])],"derivedFrom":makeQuery(id+"F2.opExtrude","SWEPT_FACE",FACE,{"disambiguationData":[OSD([subQ3])]})})});}
            var Q10;
            Q10=makeQuery(id+"F2.opExtrude","CAP_FACE",FACE,{"disambiguationData":[OSD([sQuery(id+"F0.wireOp",EDGE,"E15.MirrorCS"),sQuery(id+"F0.wireOp",EDGE,"E19.MirrorCS"),sQuery(id+"F0.wireOp",EDGE,"E21.MirrorCS"),sQuery(id+"F0.wireOp",EDGE,"E24.MirrorCS"),sQuery(id+"F0.wireOp",EDGE,"E31.MirrorCS"),sQuery(id+"F0.wireOp",EDGE,"E32.MirrorCS"),sQuery(id+"F0.wireOp",EDGE,"E34.MirrorCS"),sQuery(id+"F0.wireOp",EDGE,"E36.MirrorCS")])],"isStart":true});
            var Q11;
            {var subQ0=sQuery(id+"F0.wireOp",EDGE,"E15.MirrorCS");var subQ1=sQuery(id+"F0.wireOp",EDGE,"E21.MirrorCS");var subQ2=sQuery(id+"F0.wireOp",EDGE,"E36.MirrorCS");var subQ3=sQuery(id+"F0.wireOp",EDGE,"E32.MirrorCS");Q11=makeQuery(id+"F3.boolean.opBoolean","SPLIT",FACE,{"disambiguationData":[TD([makeQuery(id+"F2.opExtrude","CAP_FACE",FACE,{"disambiguationData":[OSD([subQ0,sQuery(id+"F0.wireOp",EDGE,"E19.MirrorCS"),subQ1,sQuery(id+"F0.wireOp",EDGE,"E24.MirrorCS"),sQuery(id+"F0.wireOp",EDGE,"E31.MirrorCS"),subQ3,sQuery(id+"F0.wireOp",EDGE,"E34.MirrorCS"),subQ2])],"isStart":false})])],"derivedFrom":makeQuery(id+"F2.opExtrude","SWEPT_FACE",FACE,{"disambiguationData":[OSD([subQ2])]})});}
            var Q12;
            {var subQ0=sQuery(id+"F0.wireOp",EDGE,"E36.MirrorCS");var subQ1=sQuery(id+"F0.wireOp",EDGE,"E32.MirrorCS");var subQ2=sQuery(id+"F0.wireOp",EDGE,"E21.MirrorCS");var subQ3=sQuery(id+"F0.wireOp",EDGE,"E15.MirrorCS");Q12=makeQuery(id+"F3.boolean.opBoolean","SPLIT",FACE,{"disambiguationData":[TD([makeQuery(id+"F2.opExtrude","CAP_FACE",FACE,{"disambiguationData":[OSD([subQ3,sQuery(id+"F0.wireOp",EDGE,"E19.MirrorCS"),subQ2,sQuery(id+"F0.wireOp",EDGE,"E24.MirrorCS"),sQuery(id+"F0.wireOp",EDGE,"E31.MirrorCS"),subQ1,sQuery(id+"F0.wireOp",EDGE,"E34.MirrorCS"),subQ0])],"isStart":false})])],"derivedFrom":makeQuery(id+"F2.opExtrude","SWEPT_FACE",FACE,{"disambiguationData":[OSD([subQ3])]})});}
            var Q13;
            Q13=makeQuery(id+"F2.opExtrude","CAP_FACE",FACE,{"disambiguationData":[OSD([sQuery(id+"F0.wireOp",EDGE,"E16.MirrorCS"),sQuery(id+"F0.wireOp",EDGE,"E17.MirrorCS"),sQuery(id+"F0.wireOp",EDGE,"E18.MirrorCS"),sQuery(id+"F0.wireOp",EDGE,"E20.MirrorCS")])],"isStart":true});
            var Q14;
            {var subQ0=sQuery(id+"F0.wireOp",EDGE,"E16.MirrorCS");var subQ2=sQuery(id+"F0.wireOp",EDGE,"E20.MirrorCS");var subQ3=sQuery(id+"F0.wireOp",EDGE,"E18.MirrorCS");var subQ4=sQuery(id+"F0.wireOp",EDGE,"E17.MirrorCS");var subQ5=makeQuery(id+"F2.opExtrude","CAP_FACE",FACE,{"disambiguationData":[OSD([subQ0,subQ4,subQ3,subQ2])],"isStart":true});Q14=makeQuery(id+"F4.boolean.opBoolean","SPLIT",FACE,{"disambiguationData":[TD([subQ5])],"derivedFrom":makeQuery(id+"F3.boolean.opBoolean","SPLIT",FACE,{"disambiguationData":[TD([subQ5])],"derivedFrom":makeQuery(id+"F2.opExtrude","SWEPT_FACE",FACE,{"disambiguationData":[OSD([subQ2])]})})});}
            var Q15;
            {var subQ0=sQuery(id+"F0.wireOp",EDGE,"E20.MirrorCS");var subQ1=sQuery(id+"F0.wireOp",EDGE,"E18.MirrorCS");var subQ2=sQuery(id+"F0.wireOp",EDGE,"E17.MirrorCS");var subQ3=sQuery(id+"F0.wireOp",EDGE,"E16.MirrorCS");var subQ4=makeQuery(id+"F2.opExtrude","CAP_FACE",FACE,{"disambiguationData":[OSD([subQ3,subQ2,subQ1,subQ0])],"isStart":true});Q15=makeQuery(id+"F4.boolean.opBoolean","SPLIT",FACE,{"disambiguationData":[TD([subQ4])],"derivedFrom":makeQuery(id+"F3.boolean.opBoolean","SPLIT",FACE,{"disambiguationData":[TD([subQ4])],"derivedFrom":makeQuery(id+"F2.opExtrude","SWEPT_FACE",FACE,{"disambiguationData":[OSD([subQ2])]})})});}
            var Q16;
            {var subQ0=sQuery(id+"F0.wireOp",EDGE,"E16.MirrorCS");var subQ2=sQuery(id+"F0.wireOp",EDGE,"E37.MirrorCS");var subQ3=sQuery(id+"F0.wireOp",EDGE,"E35.MirrorCS");var subQ4=sQuery(id+"F0.wireOp",EDGE,"E23.MirrorCS");var subQ5=sQuery(id+"F0.wireOp",EDGE,"E22.MirrorCS");var subQ6=sQuery(id+"F0.wireOp",EDGE,"E20.MirrorCS");var subQ7=sQuery(id+"F0.wireOp",EDGE,"E18.MirrorCS");var subQ8=sQuery(id+"F0.wireOp",EDGE,"E17.MirrorCS");var subQ10=makeQuery(id+"F3.opExtrude","CAP_FACE",FACE,{"disambiguationData":[OSD([subQ0,subQ8,subQ7,subQ6,subQ5,subQ4,subQ3,subQ2])],"isStart":true});Q16=makeQuery(id+"F4.boolean.opBoolean","SPLIT",FACE,{"disambiguationData":[TD([makeQuery(id+"F3.boolean.opBoolean","COPY",FACE,{"derivedFrom":subQ10})])],"derivedFrom":makeQuery(id+"F3.boolean.opBoolean","SPLIT",FACE,{"disambiguationData":[TD([makeQuery(id+"F2.opExtrude","CAP_FACE",FACE,{"disambiguationData":[OSD([subQ0,subQ8,subQ7,subQ6])],"isStart":true})])],"derivedFrom":makeQuery(id+"F2.opExtrude","SWEPT_FACE",FACE,{"disambiguationData":[OSD([subQ6])]})})});}
            var Q17;
            {var subQ0=sQuery(id+"F0.wireOp",EDGE,"E18.MirrorCS");var subQ2=sQuery(id+"F0.wireOp",EDGE,"E20.MirrorCS");var subQ4=sQuery(id+"F0.wireOp",EDGE,"E37.MirrorCS");var subQ5=sQuery(id+"F0.wireOp",EDGE,"E35.MirrorCS");var subQ6=sQuery(id+"F0.wireOp",EDGE,"E23.MirrorCS");var subQ7=sQuery(id+"F0.wireOp",EDGE,"E22.MirrorCS");var subQ8=sQuery(id+"F0.wireOp",EDGE,"E17.MirrorCS");var subQ9=sQuery(id+"F0.wireOp",EDGE,"E16.MirrorCS");var subQ10=makeQuery(id+"F3.opExtrude","CAP_FACE",FACE,{"disambiguationData":[OSD([subQ9,subQ8,subQ0,subQ2,subQ7,subQ6,subQ5,subQ4])],"isStart":true});Q17=makeQuery(id+"F4.boolean.opBoolean","SPLIT",FACE,{"disambiguationData":[TD([makeQuery(id+"F3.boolean.opBoolean","COPY",FACE,{"derivedFrom":subQ10})])],"derivedFrom":makeQuery(id+"F3.boolean.opBoolean","SPLIT",FACE,{"disambiguationData":[TD([makeQuery(id+"F2.opExtrude","CAP_FACE",FACE,{"disambiguationData":[OSD([subQ9,subQ8,subQ0,subQ2])],"isStart":true})])],"derivedFrom":makeQuery(id+"F2.opExtrude","SWEPT_FACE",FACE,{"disambiguationData":[OSD([subQ8])]})})});}
            var Q18;
            {var subQ0=sQuery(id+"F0.wireOp",EDGE,"E16.MirrorCS");var subQ1=sQuery(id+"F0.wireOp",EDGE,"E20.MirrorCS");var subQ2=sQuery(id+"F0.wireOp",EDGE,"E18.MirrorCS");var subQ3=sQuery(id+"F0.wireOp",EDGE,"E17.MirrorCS");Q18=makeQuery(id+"F3.boolean.opBoolean","SPLIT",FACE,{"disambiguationData":[TD([makeQuery(id+"F2.opExtrude","CAP_FACE",FACE,{"disambiguationData":[OSD([subQ0,subQ3,subQ2,subQ1])],"isStart":false})])],"derivedFrom":makeQuery(id+"F2.opExtrude","SWEPT_FACE",FACE,{"disambiguationData":[OSD([subQ1])]})});}
            var Q19;
            {var subQ0=sQuery(id+"F0.wireOp",EDGE,"E20.MirrorCS");var subQ1=sQuery(id+"F0.wireOp",EDGE,"E18.MirrorCS");var subQ2=sQuery(id+"F0.wireOp",EDGE,"E17.MirrorCS");var subQ3=sQuery(id+"F0.wireOp",EDGE,"E16.MirrorCS");Q19=makeQuery(id+"F3.boolean.opBoolean","SPLIT",FACE,{"disambiguationData":[TD([makeQuery(id+"F2.opExtrude","CAP_FACE",FACE,{"disambiguationData":[OSD([subQ3,subQ2,subQ1,subQ0])],"isStart":false})])],"derivedFrom":makeQuery(id+"F2.opExtrude","SWEPT_FACE",FACE,{"disambiguationData":[OSD([subQ2])]})});}
            var Q20;
            Q20=makeQuery(id+"F2.opExtrude","CAP_FACE",FACE,{"disambiguationData":[OSD([sQuery(id+"F0.wireOp",EDGE,"E16.MirrorCS"),sQuery(id+"F0.wireOp",EDGE,"E17.MirrorCS"),sQuery(id+"F0.wireOp",EDGE,"E18.MirrorCS"),sQuery(id+"F0.wireOp",EDGE,"E20.MirrorCS")])],"isStart":false});
            var Q21;
            {var subQ0=sQuery(id+"F0.wireOp",EDGE,"E16.MirrorCS");var subQ2=sQuery(id+"F0.wireOp",EDGE,"E20.MirrorCS");var subQ3=sQuery(id+"F0.wireOp",EDGE,"E18.MirrorCS");var subQ4=sQuery(id+"F0.wireOp",EDGE,"E17.MirrorCS");var subQ5=makeQuery(id+"F2.opExtrude","CAP_FACE",FACE,{"disambiguationData":[OSD([subQ0,subQ4,subQ3,subQ2])],"isStart":true});Q21=makeQuery(id+"F4.boolean.opBoolean","SPLIT",FACE,{"disambiguationData":[TD([subQ5])],"derivedFrom":makeQuery(id+"F3.boolean.opBoolean","SPLIT",FACE,{"disambiguationData":[TD([subQ5])],"derivedFrom":makeQuery(id+"F2.opExtrude","SWEPT_FACE",FACE,{"disambiguationData":[OSD([subQ3])]})})});}
            var Q22;
            {var subQ0=sQuery(id+"F0.wireOp",EDGE,"E20.MirrorCS");var subQ1=sQuery(id+"F0.wireOp",EDGE,"E18.MirrorCS");var subQ2=sQuery(id+"F0.wireOp",EDGE,"E17.MirrorCS");var subQ3=sQuery(id+"F0.wireOp",EDGE,"E16.MirrorCS");var subQ4=makeQuery(id+"F2.opExtrude","CAP_FACE",FACE,{"disambiguationData":[OSD([subQ3,subQ2,subQ1,subQ0])],"isStart":true});Q22=makeQuery(id+"F4.boolean.opBoolean","SPLIT",FACE,{"disambiguationData":[TD([subQ4])],"derivedFrom":makeQuery(id+"F3.boolean.opBoolean","SPLIT",FACE,{"disambiguationData":[TD([subQ4])],"derivedFrom":makeQuery(id+"F2.opExtrude","SWEPT_FACE",FACE,{"disambiguationData":[OSD([subQ3])]})})});}
            var Q23;
            {var subQ0=sQuery(id+"F0.wireOp",EDGE,"E18.MirrorCS");var subQ2=sQuery(id+"F0.wireOp",EDGE,"E20.MirrorCS");var subQ4=sQuery(id+"F0.wireOp",EDGE,"E37.MirrorCS");var subQ5=sQuery(id+"F0.wireOp",EDGE,"E35.MirrorCS");var subQ6=sQuery(id+"F0.wireOp",EDGE,"E23.MirrorCS");var subQ7=sQuery(id+"F0.wireOp",EDGE,"E22.MirrorCS");var subQ8=sQuery(id+"F0.wireOp",EDGE,"E17.MirrorCS");var subQ9=sQuery(id+"F0.wireOp",EDGE,"E16.MirrorCS");var subQ10=makeQuery(id+"F3.opExtrude","CAP_FACE",FACE,{"disambiguationData":[OSD([subQ9,subQ8,subQ0,subQ2,subQ7,subQ6,subQ5,subQ4])],"isStart":true});Q23=makeQuery(id+"F4.boolean.opBoolean","SPLIT",FACE,{"disambiguationData":[TD([makeQuery(id+"F3.boolean.opBoolean","COPY",FACE,{"derivedFrom":subQ10})])],"derivedFrom":makeQuery(id+"F3.boolean.opBoolean","SPLIT",FACE,{"disambiguationData":[TD([makeQuery(id+"F2.opExtrude","CAP_FACE",FACE,{"disambiguationData":[OSD([subQ9,subQ8,subQ0,subQ2])],"isStart":true})])],"derivedFrom":makeQuery(id+"F2.opExtrude","SWEPT_FACE",FACE,{"disambiguationData":[OSD([subQ9])]})})});}
            var Q24;
            {var subQ0=sQuery(id+"F0.wireOp",EDGE,"E16.MirrorCS");var subQ2=sQuery(id+"F0.wireOp",EDGE,"E37.MirrorCS");var subQ3=sQuery(id+"F0.wireOp",EDGE,"E35.MirrorCS");var subQ4=sQuery(id+"F0.wireOp",EDGE,"E23.MirrorCS");var subQ5=sQuery(id+"F0.wireOp",EDGE,"E22.MirrorCS");var subQ6=sQuery(id+"F0.wireOp",EDGE,"E20.MirrorCS");var subQ7=sQuery(id+"F0.wireOp",EDGE,"E18.MirrorCS");var subQ8=sQuery(id+"F0.wireOp",EDGE,"E17.MirrorCS");var subQ10=makeQuery(id+"F3.opExtrude","CAP_FACE",FACE,{"disambiguationData":[OSD([subQ0,subQ8,subQ7,subQ6,subQ5,subQ4,subQ3,subQ2])],"isStart":true});Q24=makeQuery(id+"F4.boolean.opBoolean","SPLIT",FACE,{"disambiguationData":[TD([makeQuery(id+"F3.boolean.opBoolean","COPY",FACE,{"derivedFrom":subQ10})])],"derivedFrom":makeQuery(id+"F3.boolean.opBoolean","SPLIT",FACE,{"disambiguationData":[TD([makeQuery(id+"F2.opExtrude","CAP_FACE",FACE,{"disambiguationData":[OSD([subQ0,subQ8,subQ7,subQ6])],"isStart":true})])],"derivedFrom":makeQuery(id+"F2.opExtrude","SWEPT_FACE",FACE,{"disambiguationData":[OSD([subQ7])]})})});}
            var Q25;
            {var subQ0=sQuery(id+"F0.wireOp",EDGE,"E16.MirrorCS");var subQ1=sQuery(id+"F0.wireOp",EDGE,"E20.MirrorCS");var subQ2=sQuery(id+"F0.wireOp",EDGE,"E18.MirrorCS");var subQ3=sQuery(id+"F0.wireOp",EDGE,"E17.MirrorCS");Q25=makeQuery(id+"F3.boolean.opBoolean","SPLIT",FACE,{"disambiguationData":[TD([makeQuery(id+"F2.opExtrude","CAP_FACE",FACE,{"disambiguationData":[OSD([subQ0,subQ3,subQ2,subQ1])],"isStart":false})])],"derivedFrom":makeQuery(id+"F2.opExtrude","SWEPT_FACE",FACE,{"disambiguationData":[OSD([subQ2])]})});}
            var Q26;
            Q26=makeQuery(id+"F2.opExtrude","CAP_EDGE",EDGE,{"disambiguationData":[OSD([sQuery(id+"F0.wireOp",EDGE,"E16.MirrorCS")])],"isStart":false});
            fillet(context, id + "F8", {"entities" : qUnion([Q0, Q1, Q2, Q3, Q4, Q5, Q6, Q7, Q8, Q9, Q10, Q11, Q12, Q13, Q14, Q15, Q16, Q17, Q18, Q19, Q20, Q21, Q22, Q23, Q24, Q25, Q26]), "radius" : 1 * mm, "tangentPropagation" : true, "allowEdgeOverflow" : false});
        }
    });
